# Revit family: Qf_Summit_AFZ2PVBIADA_Pharma_Vac_ADA_Compliant_Freezer
name_source: partatom
category: Specialty Equipment
units: mm (PartAtom-declared; Revit-internal decimal feet)

## family parameters
Always vertical = Yes
Cut with Voids When Loaded = No
Part Type = Normal
Room Calculation Point = No
Round Connector Dimension = Use Diameter
Shared = No
Work Plane-Based = No

## types (1)
- Qf_Summit_AFZ2PVBIADA_Pharma_Vac_ADA_Compliant_Freezer
    Apparent Power = 150 VA
    Conn Conduit = Yes
    Cycle = 60 Hz
    Default Elevation = 0 "
    Depth = 22.63 "
    Description = Pharma-Vac ADA Compliant Freezer
    Elec Conn Connection Height = 0 "
    Elec Conn RI Height = 0 "
    FL Amps = 1 A
    Foodservice Equipment Identifier = Yes
    Height = 32 "
    Identify Quantity as Lot = Yes
    Length = 19.75 "
    Manufacturer = Summit
    Max Overcurrent Protection = 0 A
    Min Ckt Ampacity = 0 A
    Model = AFZ2PVBIADA
    Number of Poles = 1
    Phase = 1
    Refrigerant Type = R290a
    URL = www.summitappliance.com
    URL Cutsheet = www.summitappliance.com
    Volts = 115 V
    Watts = 150 W
    Weight in Pounds = 99

## geometry (parser evidence)
native form markers: Blend x8, Sweep x2
no freeform markers — native parametric forms only
